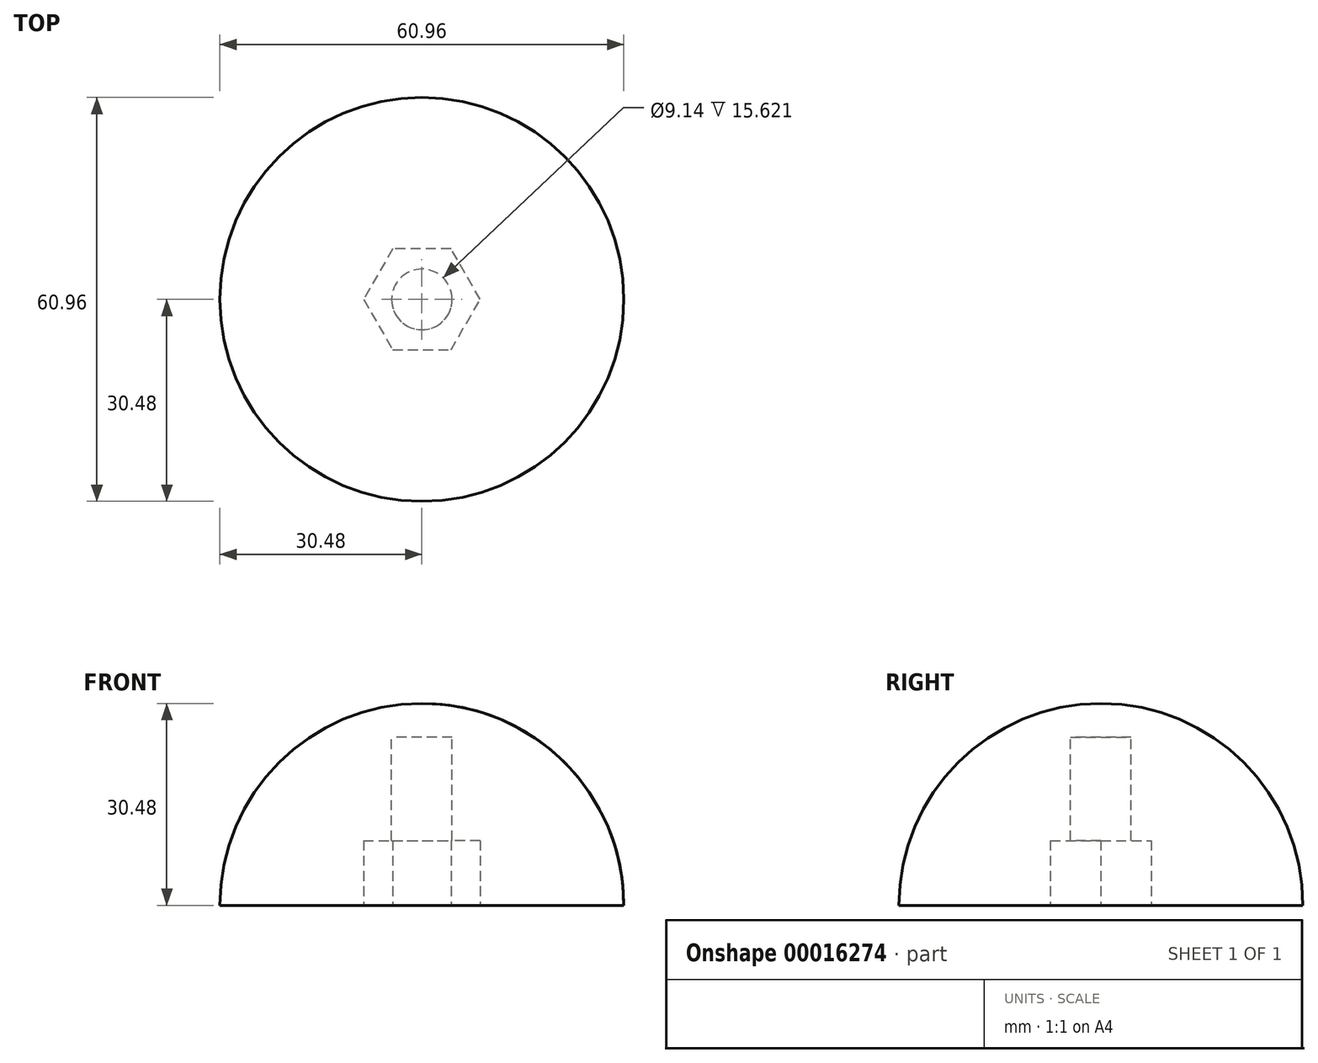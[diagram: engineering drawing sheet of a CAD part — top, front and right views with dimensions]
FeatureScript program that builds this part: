
annotation { "Feature Type Name" : "Feature", "Feature Type Description" : "" }
export const myFeature = defineFeature(function(context is Context, id is Id, definition is map)
    precondition{}
    {
        {
            var Q0;
            Q0=qCreatedBy(makeId("Front.planeOp"),FACE);
            var sketch = newSketch(context, id + "F0", { "sketchPlane" : qUnion([Q0])});
            skLineSegment(sketch, "E0", {"start": v(0, 25.4) * mm, "end": v(4.57, 25.4) * mm});
            skLineSegment(sketch, "E1", {"start": v(4.57, 0) * mm, "end": v(30.48, 0) * mm});
            skLineSegment(sketch, "E2", {"start": v(4.57, 25.4) * mm, "end": v(4.57, 0) * mm});
            skLineSegment(sketch, "E3", {"start": v(0, 25.4) * mm, "end": v(0, 30.48) * mm});
            skArc(sketch, "E4", {"start": v(30.48, 0) * mm, "mid": v(21.55, 21.55) * mm, "end": v(0, 30.48) * mm});
            skLineSegment(sketch, "E5", {"start": v(0, 23.82) * mm, "end": v(0, -13.94) * mm, "construction": true});
            skSolve(sketch);
        }
        {
            var Q0;
            Q0 = qSketchRegion(id + "F0", true);
            var Q1;
            Q1=sQuery(id+"F0.wireOp",EDGE,"E5");
            revolve(context, id + "F1", {"entities" : qUnion([Q0]), "axis" : qUnion([Q1]), "revolveType" : RevolveType.FULL});
        }
        {
            var Q0;
            Q0=makeQuery(id+"F1.opRevolve","SWEPT_FACE",FACE,{"disambiguationData":[OSD([sQuery(id+"F0.wireOp",EDGE,"E1")])]});
            var sketch = newSketch(context, id + "F2", { "sketchPlane" : qUnion([Q0])});
            skCircle(sketch, "E6.cCircle", {"center": v(0, 0) * mm, "radius": 8.8 * mm, "construction": true});
            skLineSegment(sketch, "E6.0", {"start": v(8.8, 0) * mm, "end": v(4.4, -7.62) * mm});
            skLineSegment(sketch, "E6.1", {"start": v(4.4, -7.62) * mm, "end": v(-4.4, -7.62) * mm});
            skLineSegment(sketch, "E6.2", {"start": v(-4.4, -7.62) * mm, "end": v(-8.8, 0) * mm});
            skLineSegment(sketch, "E6.3", {"start": v(-8.8, 0) * mm, "end": v(-4.4, 7.62) * mm});
            skLineSegment(sketch, "E6.4", {"start": v(-4.4, 7.62) * mm, "end": v(4.4, 7.62) * mm});
            skLineSegment(sketch, "E6.5", {"start": v(4.4, 7.62) * mm, "end": v(8.8, 0) * mm});
            skSolve(sketch);
        }
        {
            var Q0;
            Q0 = qSketchRegion(id + "F2", true);
            extrude(context, id + "F3", {"entities" : qUnion([Q0]), "operationType" : NewBodyOperationType.REMOVE, "oppositeDirection" : true, "depth" : 9.78 * mm});
        }
    });
